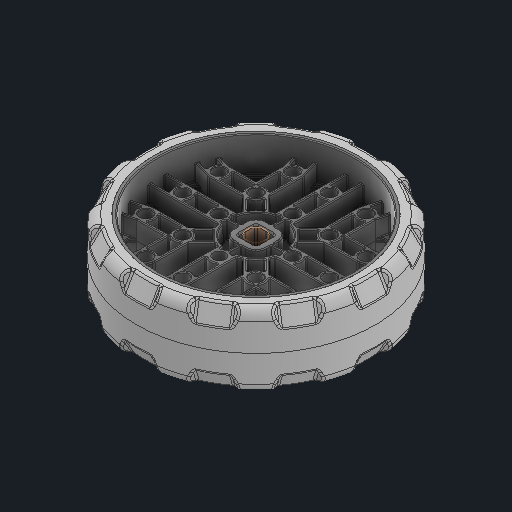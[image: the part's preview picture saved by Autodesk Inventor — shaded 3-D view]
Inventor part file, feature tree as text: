
AUTODESK INVENTOR PART (.ipt)
format: ipt  version: 2024 (Build 280153000, 153)  size: 7,958,528 bytes
history: native  units: in
note: dims shown in document units (in); Inventor stores cm internally (conversion verified against a paired STEP export)
features: other x3, extrude x1
ambient origin geometry x8: Origin, YZ Plane, XZ Plane, XY Plane, X Axis, Y Axis, Z Axis, Center Point
bodies: Solid1 (feature_tree), Solid2 (feature_tree)
feature tree (4):
  other  "Srf1"
  other  "276-7771-001 Rev4_1:1"
  other  "276-7771-002 Rev4_2:1"
  extrude  "ExtrusionSrf1"  Depth=0.3937in TaperAngle=0.0deg
